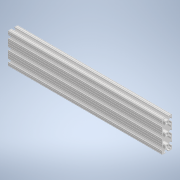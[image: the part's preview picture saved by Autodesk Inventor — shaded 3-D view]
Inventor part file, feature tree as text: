
AUTODESK INVENTOR PART (.ipt)
format: ipt  version: 2020 (Build 240168000, 168)  size: 352,768 bytes
history: native  units: in
note: dims shown in document units (in); Inventor stores cm internally (conversion verified against a paired STEP export)
features: extrude x1, sketch x1
ambient origin geometry x8: Origin, YZ Plane, XZ Plane, XY Plane, X Axis, Y Axis, Z Axis, Center Point
bodies: Solid1 (feature_tree)
feature tree (2):
  extrude  "Extrusion1"  [1 undecoded]
  sketch  "Sketch1"  dims[d0=15.0in d1=0.0in]
note: 1 required parameter value undecoded (feature->parameter linkage not recoverable at this tier; creation-order binding heuristic only, values carry confidence <= 0.55)
